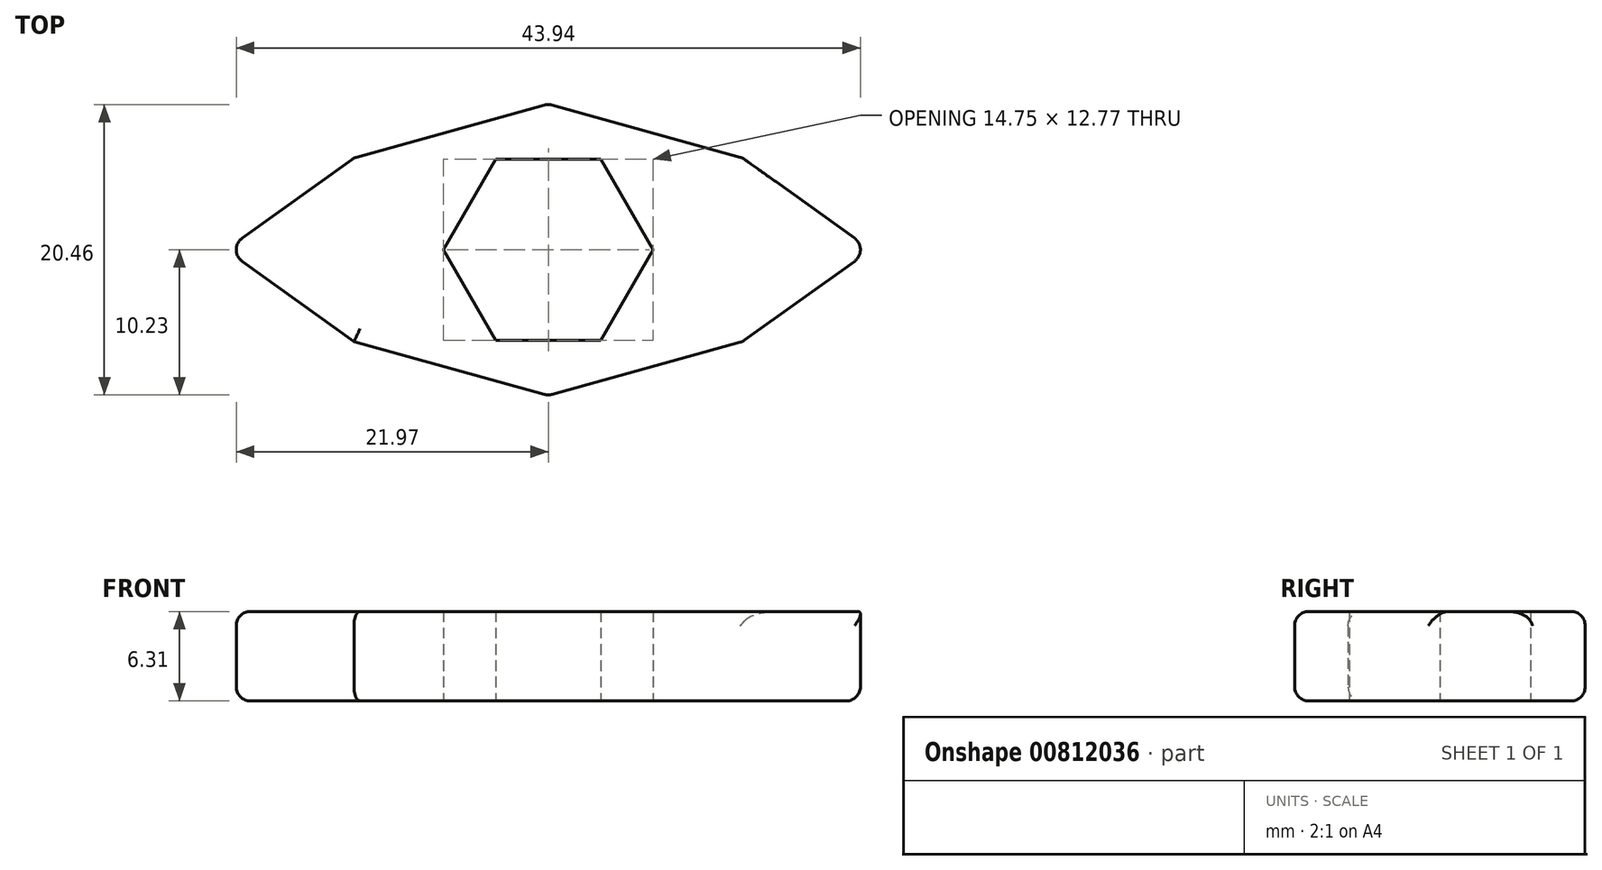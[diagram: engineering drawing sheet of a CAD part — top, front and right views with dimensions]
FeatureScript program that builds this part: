
annotation { "Feature Type Name" : "Feature", "Feature Type Description" : "" }
export const myFeature = defineFeature(function(context is Context, id is Id, definition is map)
    precondition{}
    {
        {
            var Q0;
            Q0=qCreatedBy(makeId("Top.planeOp"),FACE);
            var sketch = newSketch(context, id + "F0", { "sketchPlane" : qUnion([Q0])});
            skCircle(sketch, "E0.cCircle", {"center": v(0, 0) * mm, "radius": 6.38 * mm, "construction": true});
            skLineSegment(sketch, "E0.0", {"start": v(-3.69, 6.38) * mm, "end": v(3.69, 6.38) * mm});
            skLineSegment(sketch, "E0.1", {"start": v(3.69, 6.38) * mm, "end": v(7.37, 0) * mm});
            skLineSegment(sketch, "E0.2", {"start": v(7.37, 0) * mm, "end": v(3.69, -6.38) * mm});
            skLineSegment(sketch, "E0.3", {"start": v(3.69, -6.38) * mm, "end": v(-3.69, -6.39) * mm});
            skLineSegment(sketch, "E0.4", {"start": v(-3.69, -6.39) * mm, "end": v(-7.37, 0) * mm});
            skLineSegment(sketch, "E0.5", {"start": v(-7.37, 0) * mm, "end": v(-3.69, 6.38) * mm});
            skPoint(sketch, "E0.0.midPoint", {"position": v(0, 6.38) * mm});
            skLineSegment(sketch, "E1", {"start": v(0, 10.27) * mm, "end": v(-13.69, 6.47) * mm});
            skLineSegment(sketch, "E2", {"start": v(-13.69, 6.47) * mm, "end": v(-22.69, 0) * mm});
            skLineSegment(sketch, "E3.MirrorCS", {"start": v(0, 10.27) * mm, "end": v(13.69, 6.47) * mm});
            skLineSegment(sketch, "E4.MirrorCS", {"start": v(13.69, 6.47) * mm, "end": v(22.69, 0) * mm});
            skLineSegment(sketch, "E5.MirrorCS", {"start": v(-13.69, -6.47) * mm, "end": v(-22.69, 0) * mm});
            skLineSegment(sketch, "E6.MirrorCS", {"start": v(0, -10.27) * mm, "end": v(-13.69, -6.47) * mm});
            skLineSegment(sketch, "E7.MirrorCS", {"start": v(0, -10.27) * mm, "end": v(13.69, -6.47) * mm});
            skLineSegment(sketch, "E8.MirrorCS", {"start": v(13.69, -6.47) * mm, "end": v(22.69, 0) * mm});
            skSolve(sketch);
        }
        {
            var Q0;
            Q0 = qSketchRegion(id + "F0", true);
            extrude(context, id + "F1", {"entities" : qUnion([Q0]), "depth" : 6.3 * mm, "offsetDistance" : 25 * mm});
        }
        {
            var Q0;
            Q0=makeQuery(id+"F1.opExtrude","SWEPT_EDGE",EDGE,{"disambiguationData":[OSD([sQuery(id+"F0.wireOp",EDGE,"E2"),sQuery(id+"F0.wireOp",EDGE,"E5.MirrorCS")])]});
            var Q1;
            Q1=makeQuery(id+"F1.opExtrude","SWEPT_EDGE",EDGE,{"disambiguationData":[OSD([sQuery(id+"F0.wireOp",EDGE,"E4.MirrorCS"),sQuery(id+"F0.wireOp",EDGE,"E8.MirrorCS")])]});
            var Q2;
            Q2=makeQuery(id+"F1.opExtrude","SWEPT_EDGE",EDGE,{"disambiguationData":[OSD([sQuery(id+"F0.wireOp",EDGE,"E7.MirrorCS"),sQuery(id+"F0.wireOp",EDGE,"E8.MirrorCS")])]});
            var Q3;
            Q3=makeQuery(id+"F1.opExtrude","SWEPT_EDGE",EDGE,{"disambiguationData":[OSD([sQuery(id+"F0.wireOp",EDGE,"E6.MirrorCS"),sQuery(id+"F0.wireOp",EDGE,"E7.MirrorCS")])]});
            var Q4;
            Q4=makeQuery(id+"F1.opExtrude","CAP_EDGE",EDGE,{"disambiguationData":[OSD([sQuery(id+"F0.wireOp",EDGE,"E5.MirrorCS")])],"isStart":true});
            var Q5;
            Q5=makeQuery(id+"F1.opExtrude","SWEPT_EDGE",EDGE,{"disambiguationData":[OSD([sQuery(id+"F0.wireOp",EDGE,"E1"),sQuery(id+"F0.wireOp",EDGE,"E3.MirrorCS")])]});
            var Q6;
            Q6=makeQuery(id+"F1.opExtrude","SWEPT_EDGE",EDGE,{"disambiguationData":[OSD([sQuery(id+"F0.wireOp",EDGE,"E3.MirrorCS"),sQuery(id+"F0.wireOp",EDGE,"E4.MirrorCS")])]});
            var Q7;
            Q7=makeQuery(id+"F1.opExtrude","SWEPT_EDGE",EDGE,{"disambiguationData":[OSD([sQuery(id+"F0.wireOp",EDGE,"E1"),sQuery(id+"F0.wireOp",EDGE,"E2")])]});
            var Q8;
            Q8=makeQuery(id+"F1.opExtrude","CAP_EDGE",EDGE,{"disambiguationData":[OSD([sQuery(id+"F0.wireOp",EDGE,"E1")])],"isStart":true});
            var Q9;
            Q9=makeQuery(id+"F1.opExtrude","CAP_EDGE",EDGE,{"disambiguationData":[OSD([sQuery(id+"F0.wireOp",EDGE,"E3.MirrorCS")])],"isStart":false});
            var Q10;
            Q10=makeQuery(id+"F1.opExtrude","CAP_EDGE",EDGE,{"disambiguationData":[OSD([sQuery(id+"F0.wireOp",EDGE,"E3.MirrorCS")])],"isStart":true});
            var Q11;
            Q11=makeQuery(id+"F1.opExtrude","CAP_EDGE",EDGE,{"disambiguationData":[OSD([sQuery(id+"F0.wireOp",EDGE,"E4.MirrorCS")])],"isStart":true});
            var Q12;
            Q12=makeQuery(id+"F1.opExtrude","CAP_EDGE",EDGE,{"disambiguationData":[OSD([sQuery(id+"F0.wireOp",EDGE,"E8.MirrorCS")])],"isStart":false});
            var Q13;
            Q13=makeQuery(id+"F1.opExtrude","CAP_EDGE",EDGE,{"disambiguationData":[OSD([sQuery(id+"F0.wireOp",EDGE,"E7.MirrorCS")])],"isStart":false});
            var Q14;
            Q14=makeQuery(id+"F1.opExtrude","CAP_EDGE",EDGE,{"disambiguationData":[OSD([sQuery(id+"F0.wireOp",EDGE,"E6.MirrorCS")])],"isStart":false});
            var Q15;
            Q15=makeQuery(id+"F1.opExtrude","CAP_EDGE",EDGE,{"disambiguationData":[OSD([sQuery(id+"F0.wireOp",EDGE,"E5.MirrorCS")])],"isStart":false});
            var Q16;
            Q16=makeQuery(id+"F1.opExtrude","CAP_EDGE",EDGE,{"disambiguationData":[OSD([sQuery(id+"F0.wireOp",EDGE,"E1")])],"isStart":false});
            var Q17;
            Q17=makeQuery(id+"F1.opExtrude","CAP_EDGE",EDGE,{"disambiguationData":[OSD([sQuery(id+"F0.wireOp",EDGE,"E2")])],"isStart":false});
            var Q18;
            Q18=makeQuery(id+"F1.opExtrude","CAP_EDGE",EDGE,{"disambiguationData":[OSD([sQuery(id+"F0.wireOp",EDGE,"E2")])],"isStart":true});
            var Q19;
            Q19=makeQuery(id+"F1.opExtrude","CAP_EDGE",EDGE,{"disambiguationData":[OSD([sQuery(id+"F0.wireOp",EDGE,"E7.MirrorCS")])],"isStart":true});
            var Q20;
            Q20=makeQuery(id+"F1.opExtrude","CAP_EDGE",EDGE,{"disambiguationData":[OSD([sQuery(id+"F0.wireOp",EDGE,"E6.MirrorCS")])],"isStart":true});
            var Q21;
            Q21=makeQuery(id+"F1.opExtrude","CAP_EDGE",EDGE,{"disambiguationData":[OSD([sQuery(id+"F0.wireOp",EDGE,"E8.MirrorCS")])],"isStart":true});
            fillet(context, id + "F2", {"entities" : qUnion([Q0, Q1, Q2, Q3, Q4, Q5, Q6, Q7, Q8, Q9, Q10, Q11, Q12, Q13, Q14, Q15, Q16, Q17, Q18, Q19, Q20, Q21]), "radius" : 1 * mm, "tangentPropagation" : true, "allowEdgeOverflow" : false});
        }
    });
